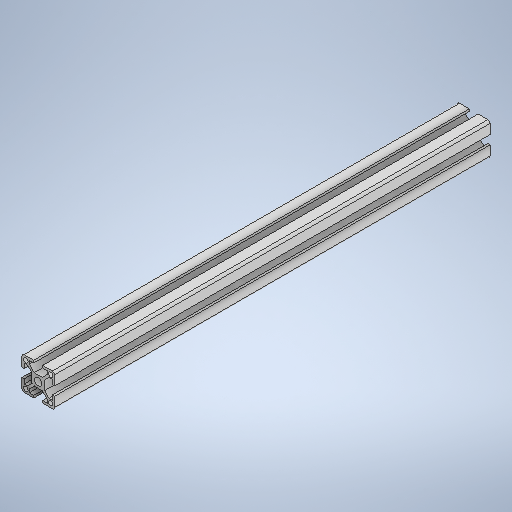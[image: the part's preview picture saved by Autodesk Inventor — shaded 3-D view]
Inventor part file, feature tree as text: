
AUTODESK INVENTOR PART (.ipt)
format: ipt  version: 2025 (Build 290162000, 162)  size: 314,880 bytes
history: native  units: in
note: dims shown in document units (in); Inventor stores cm internally (conversion verified against a paired STEP export)
features: extrude x1, sketch x1
ambient origin geometry x8: Origin, YZ Plane, XZ Plane, XY Plane, X Axis, Y Axis, Z Axis, Center Point
bodies: Solid1 (feature_tree)
feature tree (2):
  extrude  "Extrusion1"  Depth=15.748in
  sketch  "Sketch1"  dims[d6=15.748in d7=0.0in d8=0.1969in d9=0.0344in d10=0.1969in d11=0.0344in]
